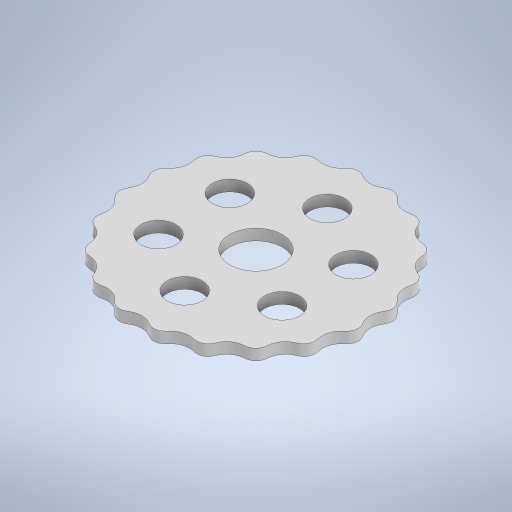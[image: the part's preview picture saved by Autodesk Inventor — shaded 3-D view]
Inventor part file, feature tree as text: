
AUTODESK INVENTOR PART (.ipt)
format: ipt  version: 2023 (Build 270158000, 158)  size: 358,400 bytes
history: native  units: in
note: dims shown in document units (in); Inventor stores cm internally (conversion verified against a paired STEP export)
features: extrude x2, sketch x2, other x1
ambient origin geometry x8: Origin, YZ Plane, XZ Plane, XY Plane, X Axis, Y Axis, Z Axis, Center Point
bodies: Body1 (feature_tree)
feature tree (5):
  extrude  "Extrusion2"  Depth=0.1969in TaperAngle=0.0deg
  extrude  "Extrusion3"  Depth=0.6299in
  sketch  "Sketch2"  dims[d6=0.0in d7=141.3386in d8=0.1969in d9=0.0in]
  other  "2D Equation Curve3"
  sketch  "Sketch3"  dims[d10=0.9449in d11=0.6299in d12=2.5591in d13=2.3622in d15=360.0deg d17=0.0in d18=0.0in d20=0.5709in d21=0.8661in]
